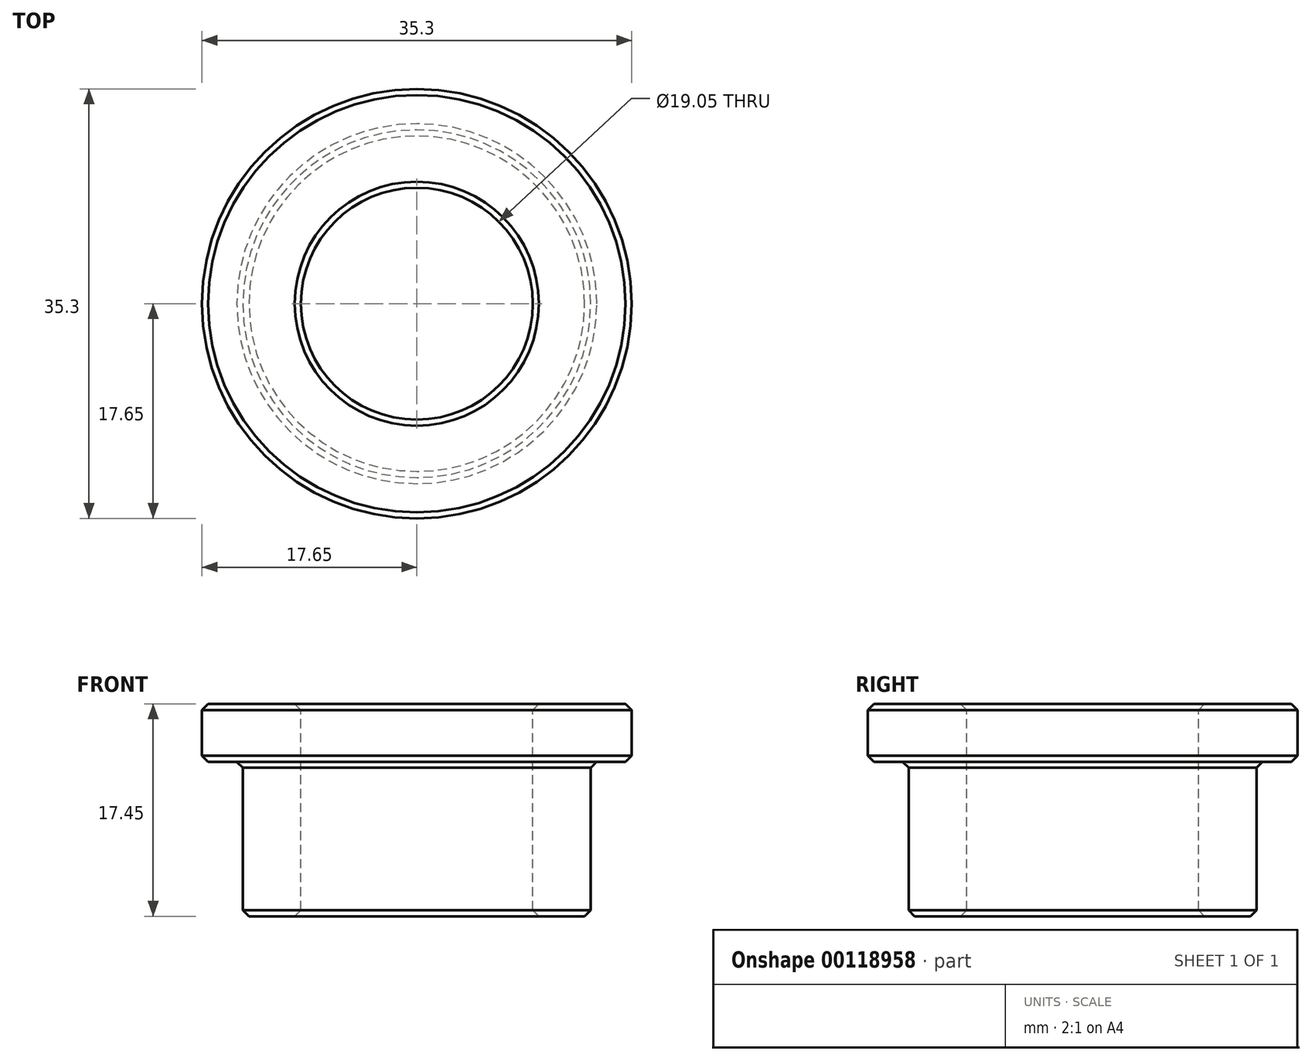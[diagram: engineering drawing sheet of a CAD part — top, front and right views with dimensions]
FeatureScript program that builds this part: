
annotation { "Feature Type Name" : "Feature", "Feature Type Description" : "" }
export const myFeature = defineFeature(function(context is Context, id is Id, definition is map)
    precondition{}
    {
        {
            var Q0;
            Q0=qCreatedBy(makeId("Top.planeOp"),FACE);
            var sketch = newSketch(context, id + "F0", { "sketchPlane" : qUnion([Q0])});
            skCircle(sketch, "E0", {"center": v(0, 0) * mm, "radius": 14.29 * mm});
            skCircle(sketch, "E1", {"center": v(0, 0) * mm, "radius": 9.53 * mm});
            skSolve(sketch);
        }
        {
            var Q0;
            Q0=makeQuery(id+"F0.imprint","IMPRINT",FACE,{"disambiguationData":[TD([[makeQuery(id+"F0.imprint","IMPRINT",EDGE,{"derivedFrom":sQuery(id+"F0.wireOp",EDGE,"E0")}),1.0]])]});
            extrude(context, id + "F1", {"entities" : qUnion([Q0]), "oppositeDirection" : true, "depth" : 12.7 * mm});
        }
        {
            var Q0;
            Q0=qCreatedBy(makeId("Top.planeOp"),FACE);
            var sketch = newSketch(context, id + "F2", { "sketchPlane" : qUnion([Q0])});
            skCircle(sketch, "E2.0", {"center": v(0, 0) * mm, "radius": 9.53 * mm});
            skCircle(sketch, "E3", {"center": v(0, 0) * mm, "radius": 17.65 * mm});
            skSolve(sketch);
        }
        {
            var Q0;
            Q0=qSketchRegion(id+"F2",true);
            extrude(context, id + "F3", {"entities" : qUnion([Q0]), "operationType" : NewBodyOperationType.ADD, "depth" : 4.75 * mm});
        }
        {
            var Q0;
            Q0=makeQuery(id+"F3.opExtrude","SWEPT_FACE",FACE,{"disambiguationData":[OSD([sQuery(id+"F2.wireOp",EDGE,"E3")])]});
            var Q1;
            Q1=makeQuery(id+"F3.boolean.opBoolean","MERGE",FACE,{"derivedFrom":[makeQuery(id+"F1.opExtrude","SWEPT_FACE",FACE,{"disambiguationData":[OSD([sQuery(id+"F0.wireOp",EDGE,"E1")])]}),makeQuery(id+"F3.opExtrude","SWEPT_FACE",FACE,{"disambiguationData":[OSD([sQuery(id+"F2.wireOp",EDGE,"E2.0")])]})]});
            var Q2;
            Q2=makeQuery(id+"F1.opExtrude","SWEPT_FACE",FACE,{"disambiguationData":[OSD([sQuery(id+"F0.wireOp",EDGE,"E0")])]});
            chamfer(context, id + "F4", {"entities" : qUnion([Q0, Q1, Q2]), "width" : 0.5 * mm, "tangentPropagation" : true});
        }
    });
